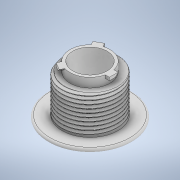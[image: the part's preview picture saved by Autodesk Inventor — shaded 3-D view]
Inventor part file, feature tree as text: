
AUTODESK INVENTOR PART (.ipt)
format: ipt  version: 2020.2 (Build 242310000, 310)  size: 737,792 bytes
history: native  units: mm
features: sketch x8, extrude x3, revolve x2, fillet x1, pattern_circular x1, thread x1, helix x1
ambient origin geometry x8: Origin, YZ Plane, XZ Plane, XY Plane, X Axis, Y Axis, Z Axis, Center Point
bodies: Solid1 (feature_tree), Solid5 (feature_tree)
feature tree (17):
  extrude  "Extrusion1"  Depth=2.0mm
  fillet  "Fillet1"  [1 undecoded]
  pattern_circular  "Circular Pattern1"  Count=3  [1 undecoded]
  extrude  "Extrusion5"  TaperAngle=0.0deg  [1 undecoded]
  thread  "Thread4"  [1 undecoded]
  sketch  "Sketch15"  dims[d22=0.0mm d23=0.0mm d33=9.599311mm]
  revolve  "Revolution7"  [1 undecoded]
  revolve  "Revolution8"  Angle=360.0deg
  helix  "Coil4"  [1 undecoded]
  sketch  "Sketch1"  dims[d0=45.0mm d1=2.0mm d2=0.0mm d3=30.0mm]
  sketch  "Sketch2"  dims[d4=20.0mm d5=0.0mm d6=1.0mm]
  sketch  "Sketch3"  dims[d7=21.5mm d8=5.0mm]
  sketch  "Sketch5"  dims[d10=0.15mm d11=2.35mm d12=3.2mm d13=1.65mm d14=2.35mm d16=0.0mm d17=12.75mm d18=30.0mm d19=360.0deg d21=18.5mm]
  sketch  "Sketch16"  dims[d54=9.599311mm]
  sketch  "Sketch17"  dims[d75=9.599311mm d87=20.0mm d88=0.0mm d89=9.599311mm d90=0.320166mm d91=0.320166mm d94=2.0mm d96=9.599311mm d98=0.0mm d99=0.0mm d100=2.002mm d101=20.0mm d102=10.0mm d103=0.0mm d104=0.0mm d105=0.0mm d106=0.0mm d107=0.0mm]
  sketch  "Sketch4"  dims[d9=0.0mm]
  extrude  "Bayonet Tab"  Depth=9.599311mm
note: 6 required parameter values undecoded (feature->parameter linkage not recoverable at this tier; creation-order binding heuristic only, values carry confidence <= 0.55)